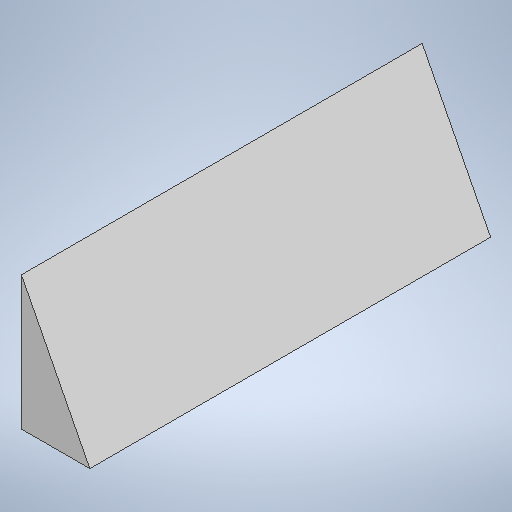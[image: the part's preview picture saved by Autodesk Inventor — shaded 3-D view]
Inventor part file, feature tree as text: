
AUTODESK INVENTOR PART (.ipt)
format: ipt  version: 2025.1 (Build 291241000, 241)  size: 186,880 bytes
history: native  units: mm
features: other x1, extrude x1, sketch x1
ambient origin geometry x8: Origin, YZ Plane, XZ Plane, XY Plane, X Axis, Y Axis, Z Axis, Center Point
bodies: Body1 (feature_tree)
feature tree (3):
  other  "Sólido1"
  extrude  "Extrusión1"  Depth=2.5mm
  sketch  "Boceto1"  dims[d0=1.281mm d1=2.5mm d2=7.5mm d3=0.0mm]
